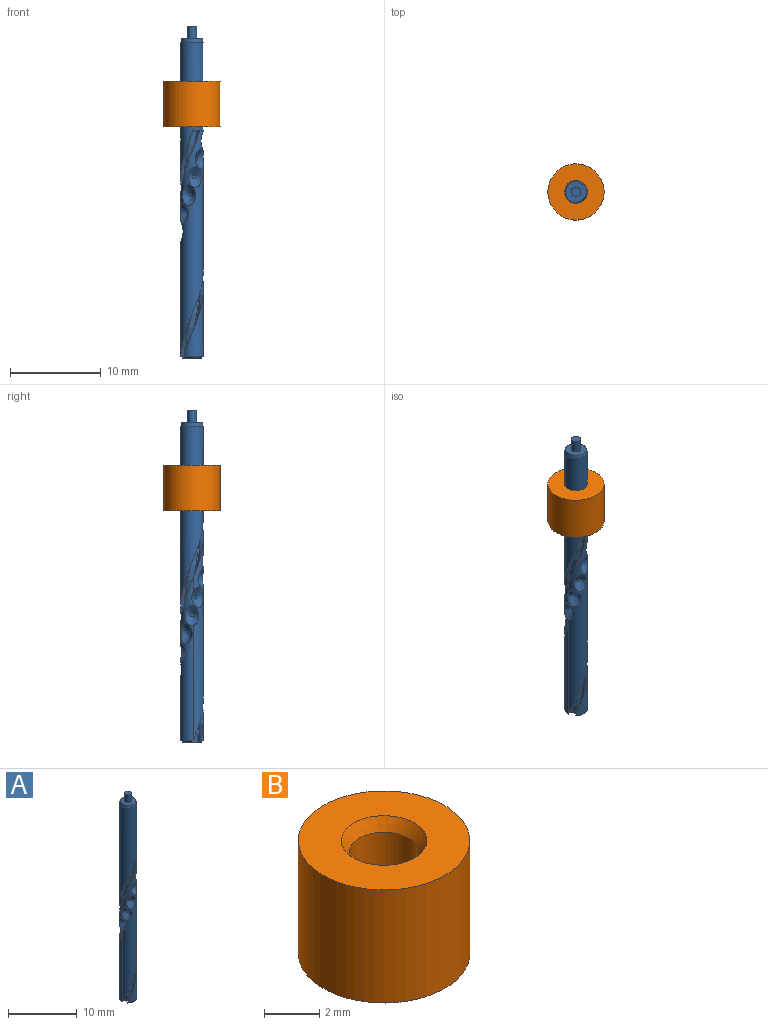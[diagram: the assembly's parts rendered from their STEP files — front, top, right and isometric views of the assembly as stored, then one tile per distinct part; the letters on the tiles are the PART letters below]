
ASSEMBLY  parts=2 mates=1
PART A: 37 faces, bbox 3.4x3.3x37.5 mm
  f0: cylinder r=1.25mm len=34.64mm, axis (0,0,-1), area 173mm2, adj f1,f4,f6,f8,f10,f20,f21,f23
  f1: cylinder r=1.25mm len=17.87mm, axis (0,0,-1), area 49.4mm2, adj f0,f10,f12,f14,f16,f18,f20,f23
  f2: plane 2.2x2.2mm, normal (0,0,-1), area 2.4mm2, adj f23,f24,f25,f26,f27,f35,f36
  f3: plane 0.4x0.4mm, normal (1,0,0), area 0.1mm2, adj f4
  f4: cone r=0.2mm half-angle=55deg, axis (1,0,0), area 3.2mm2, adj f0,f3
  f5: plane 0.4x0.38mm, normal (-0.31,-0.95,0), area 0.1mm2, adj f6
  f6: cone r=0.2mm half-angle=55deg, axis (-0.31,-0.95,0), area 3.2mm2, adj f0,f5
  f7: plane 0.4x0.38mm, normal (0.31,-0.95,0), area 0.1mm2, adj f8
  f8: cone r=0.2mm half-angle=55deg, axis (0.31,-0.95,0), area 3.2mm2, adj f0,f7
  f9: plane 0.4x0.32mm, normal (-0.81,-0.59,0), area 0.1mm2, adj f10
  f10: cone r=0.2mm half-angle=55deg, axis (-0.81,-0.59,0), area 3.4mm2, adj f0,f1,f9
  f11: plane 0.4x0.32mm, normal (0.81,0.59,0), area 0.1mm2, adj f12
  f12: cone r=0.2mm half-angle=55deg, axis (0.81,0.59,0), area 3.2mm2, adj f1,f11
  f13: plane 0.4x0.38mm, normal (0.31,0.95,0), area 0.1mm2, adj f14
  f14: cone r=0.2mm half-angle=55deg, axis (0.31,0.95,0), area 3.2mm2, adj f1,f13
  f15: plane 0.4x0.38mm, normal (-0.31,0.95,0), area 0.1mm2, adj f16
  f16: cone r=0.2mm half-angle=55deg, axis (-0.31,0.95,0), area 3.2mm2, adj f1,f15
  f17: plane 0.4x0.32mm, normal (-0.81,0.59,0), area 0.1mm2, adj f18
  f18: cone r=0.2mm half-angle=55deg, axis (-0.81,0.59,0), area 3.3mm2, adj f1,f17
  f19: plane 0.4x0.4mm, normal (-1,0,0), area 0.1mm2, adj f20
  f20: cone r=0.2mm half-angle=55deg, axis (-1,0,0), area 3.3mm2, adj f0,f1,f19
  f21: cone r=0.2mm half-angle=55deg, axis (0.81,-0.59,0), area 3.2mm2, adj f0,f22
  f22: plane 0.4x0.32mm, normal (0.81,-0.59,0), area 0.1mm2, adj f21
  f23: bspline ~26x2.61mm, area 11.3mm2, adj f0,f1,f2,f24,f29,f36
  f24: bspline ~26x1.8mm, area 4mm2, adj f2,f23,f25,f29
  f25: bspline ~26x1.51mm, area 15.6mm2, adj f2,f24,f26,f29
  f26: bspline ~26x1.79mm, area 4mm2, adj f2,f25,f27,f29
  f27: bspline ~25.1x2.5mm, area 11.3mm2, adj f0,f2,f26,f29,f36
  f28: plane 2.28x2.28mm, normal (0,0,1), area 3.3mm2, adj f30,f32
  f29: plane 0.94x0.79mm, normal (0,0,-1), area 0.5mm2, adj f0,f23,f24,f25,f26,f27
  f30: cylinder r=0.5mm len=1.4mm, axis (0,0,-1), area 4.4mm2, adj f28,f31
  f31: plane 1x1mm, normal (0,0,1), area 0.8mm2, adj f30
  f32: cone r=1.14mm half-angle=15deg, axis (0,0,-1), area 3.2mm2, adj f0,f28
  f33: cylinder r=0.4mm len=1.9mm, axis (0,0,-1), area 4.8mm2, adj f34,f35
  f34: plane 0.8x0.8mm, normal (0,0,-1), area 0.5mm2, adj f33
  f35: cone r=0.4mm half-angle=60deg, axis (0,0,-1), area 0.6mm2, adj f2,f33
  f36: cone r=1.25mm half-angle=45deg, axis (0,0,1), area 1.4mm2, adj f1,f2,f23,f27
PART B: 5 faces, bbox 6.2x6.2x5 mm
  f0: cylinder r=1.25mm len=4.48mm, axis (0,0,-1), area 35.2mm2, adj f3,f4
  f1: cylinder r=3.1mm len=6.2mm, axis (0,0,-1), area 97.4mm2, adj f2,f3
  f2: plane 6.2x6.2mm, normal (0,0,1), area 22.6mm2, adj f1,f4
  f3: plane 6.2x6.2mm, normal (0,0,-1), area 25.3mm2, adj f0,f1
  f4: cone r=1.25mm half-angle=30deg, axis (0,0,1), area 5.3mm2, adj f0,f2
PLACE A at identity fixed
PLACE B rot(axis=(0,1,0),180deg) t=(0,0,30.5)mm
MATE fastened B.f0 <-> A.f0  axis (0,0,-1) through (0,0,25.5)mm
